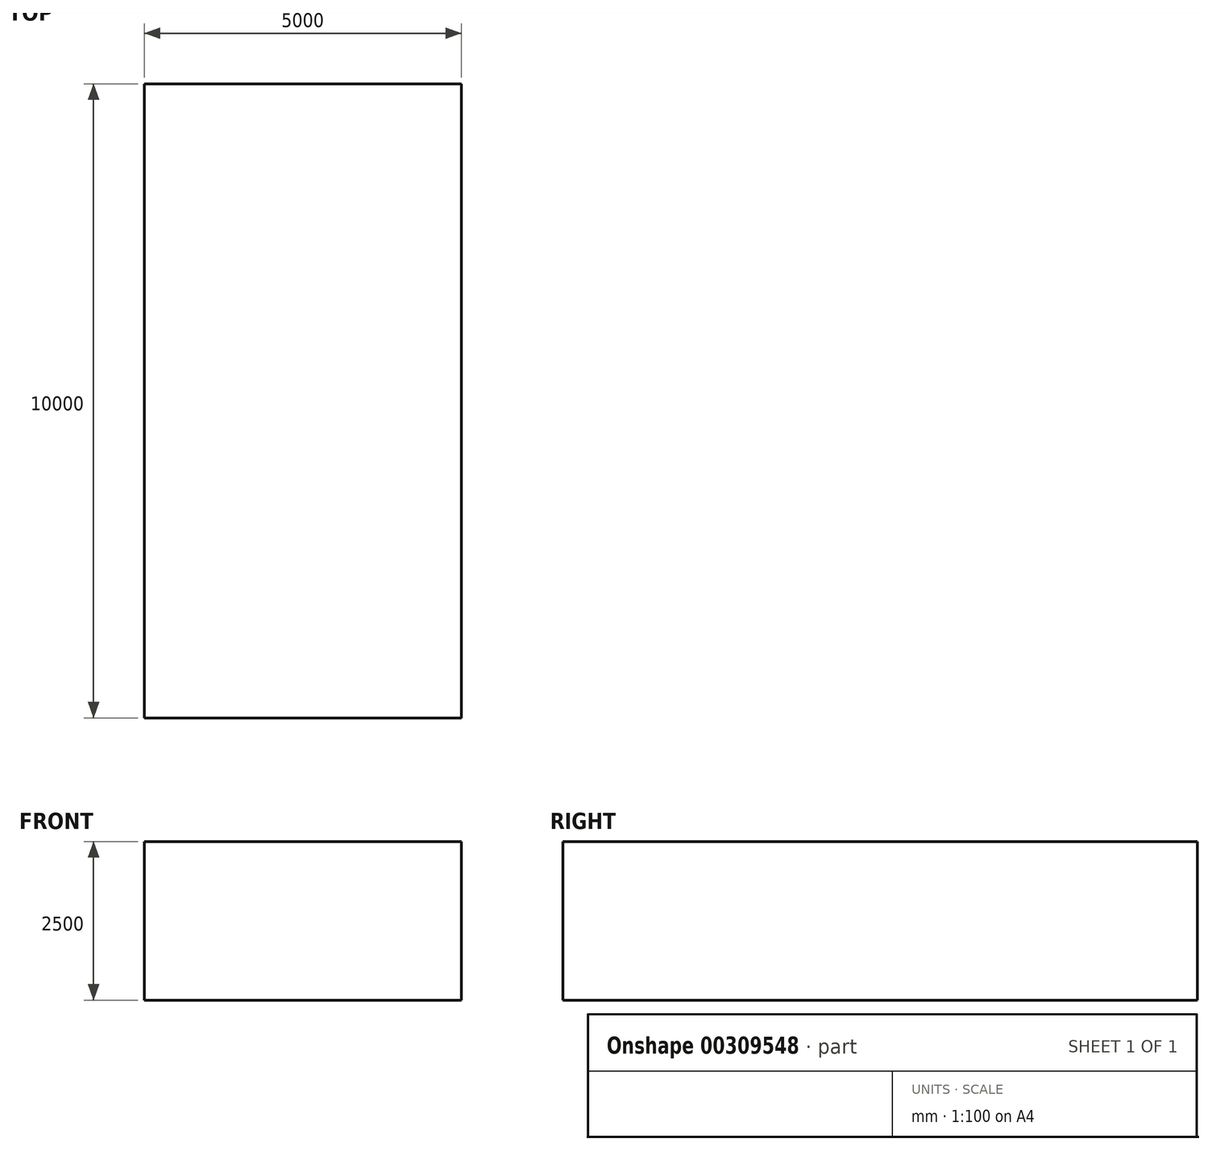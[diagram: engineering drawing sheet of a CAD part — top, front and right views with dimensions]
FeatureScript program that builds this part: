
annotation { "Feature Type Name" : "Feature", "Feature Type Description" : "" }
export const myFeature = defineFeature(function(context is Context, id is Id, definition is map)
    precondition{}
    {
        {
            var Q0;
            Q0=qCreatedBy(makeId("Front.planeOp"),FACE);
            var sketch = newSketch(context, id + "F0", { "sketchPlane" : qUnion([Q0])});
            skLineSegment(sketch, "E0.bottom", {"start": v(-2500, 1308.84) * mm, "end": v(2500, 1308.84) * mm});
            skLineSegment(sketch, "E0.top", {"start": v(-2500, -1191.16) * mm, "end": v(2500, -1191.16) * mm});
            skLineSegment(sketch, "E0.left", {"start": v(-2500, 1308.84) * mm, "end": v(-2500, -1191.16) * mm});
            skLineSegment(sketch, "E0.right", {"start": v(2500, 1308.84) * mm, "end": v(2500, -1191.16) * mm});
            skSolve(sketch);
        }
        {
            var Q0;
            Q0=makeQuery(id+"F0.imprint","IMPRINT",FACE,{"disambiguationData":[TD([[makeQuery(id+"F0.imprint","IMPRINT",EDGE,{"derivedFrom":sQuery(id+"F0.wireOp",EDGE,"E0.bottom")}),-1.0]])]});
            extrude(context, id + "F1", {"entities" : qUnion([Q0]), "depth" : 10000 * mm});
        }
    });
